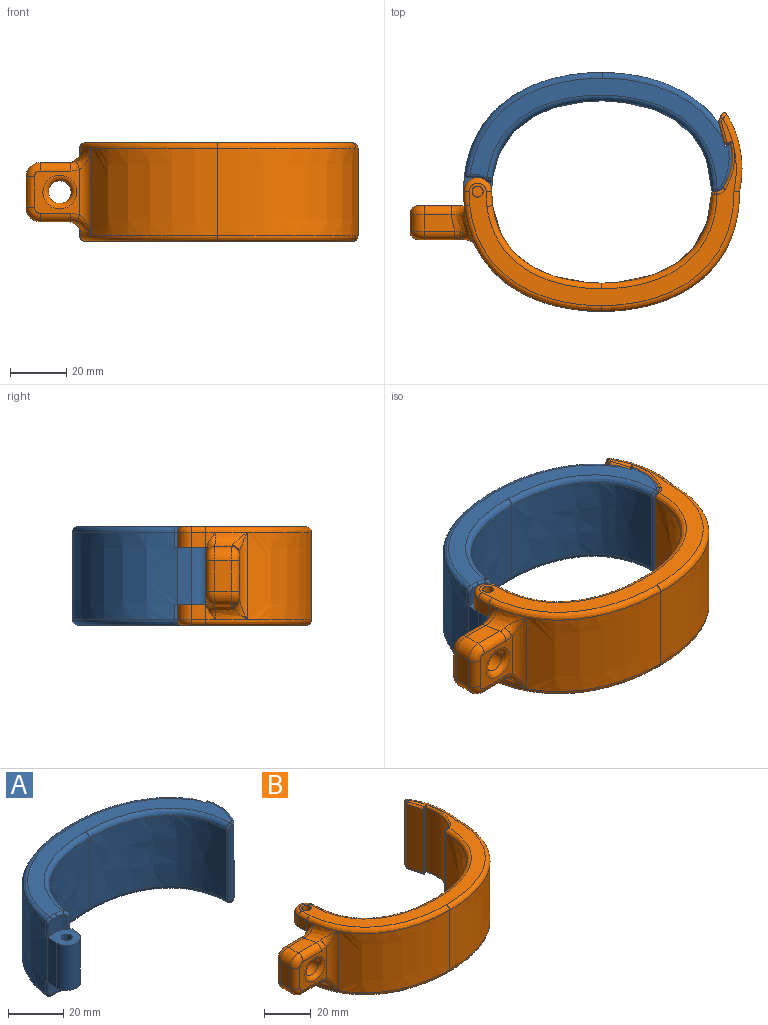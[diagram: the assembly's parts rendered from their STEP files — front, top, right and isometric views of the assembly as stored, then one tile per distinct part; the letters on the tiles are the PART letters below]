
ASSEMBLY  parts=2 mates=1
PART A: 57 faces, bbox 98.1x59.6x36.4 mm
  f0: extruded ~20x5mm, area 100.2mm2, adj f1,f12,f16,f19
  f1: cylinder r=5mm len=20mm, axis (0,0,-1), area 314.2mm2, adj f0,f3,f16,f19
  f2: cylinder r=1.95mm len=20mm, axis (0,0,-1), area 245mm2, adj f16,f19
  f3: extruded ~31x5mm, area 109.4mm2, adj f1,f4,f16,f19,f25,f30,f36,f42
  f4: extruded ~38.7x31mm, area 1624.9mm2, adj f3,f5,f24,f29
  f5: extruded ~38.98x31.03mm, area 1734.8mm2, adj f4,f23,f28,f47
  f6: plane 32.71x0.48mm, normal (0,-1,0), area 15.5mm2, adj f7,f46,f47,f49
  f7: cylinder r=3mm len=33mm, axis (0,0,-1), area 111.7mm2, adj f6,f8,f44,f45,f46,f49,f50,f51
  f8: cylinder r=20mm len=33mm, axis (0,0,-1), area 524.6mm2, adj f7,f43,f48,f54
  f9: plane 34.6x1.62mm, normal (-0.4,0.92,0), area 60.9mm2, adj f10,f52,f53,f54,f55,f56
  f10: plane 36.2x9.58mm, normal (0.96,0.27,0), area 292.8mm2, adj f9,f11,f13,f14,f22,f27,f52,f56
  f11: extruded ~41.39x31mm, area 1446.8mm2, adj f10,f12,f22,f27
  f12: extruded ~48.76x37.5mm, area 2099.6mm2, adj f0,f11,f16,f19,f21,f26,f31,f37
  f13: plane 91.85x39.01mm, normal (0,0,1), area 717.6mm2, adj f10,f26,f27,f28,f29,f30,f33,f34
  f14: plane 91.85x39.02mm, normal (0,0,-1), area 717.6mm2, adj f10,f21,f22,f23,f24,f25,f39,f40
  f15: plane 6.5x3.64mm, normal (0,-1,0), area 23.5mm2, adj f16,f17,f31,f32,f33
  f16: plane 11.2x10.29mm, normal (0,0,1), area 73.4mm2, adj f0,f1,f2,f3,f12,f15,f17,f31
  f17: cylinder r=5mm len=6.5mm, axis (0,0,-1), area 24.8mm2, adj f15,f16,f34,f35,f36
  f18: cylinder r=5mm len=6.5mm, axis (0,0,1), area 24.8mm2, adj f19,f20,f40,f41,f42
  f19: plane 11.2x10.29mm, normal (0,0,-1), area 73.4mm2, adj f0,f1,f2,f3,f12,f18,f20,f37
  f20: plane 6.5x3.64mm, normal (0,-1,0), area 23.5mm2, adj f18,f19,f37,f38,f39
  f21: bspline ~51.67x37.47mm, area 207mm2, adj f12,f14,f22,f38
  f22: bspline ~57.81x25.32mm, area 152.8mm2, adj f10,f11,f14,f21
  f23: bspline ~50.93x33.4mm, area 179.4mm2, adj f5,f14,f24,f49,f51
  f24: bspline ~50.38x45.92mm, area 168mm2, adj f4,f14,f23,f25
  f25: bspline ~2.68x2.27mm, area 1.9mm2, adj f3,f14,f24,f41
  f26: bspline ~51.67x37.47mm, area 207mm2, adj f12,f13,f27,f32
  f27: bspline ~57.81x25.32mm, area 152.8mm2, adj f10,f11,f13,f26
  f28: bspline ~50.93x33.4mm, area 179.4mm2, adj f5,f13,f29,f45,f46
  f29: bspline ~53.82x50.38mm, area 168mm2, adj f4,f13,f28,f30
  f30: bspline ~2.68x2.27mm, area 1.9mm2, adj f3,f13,f29,f35
  f31: cylinder r=1mm len=5.5mm, axis (0,0,-1), area 9.3mm2, adj f12,f15,f16,f32
  f32: bspline ~2.48x2.25mm, area 4.3mm2, adj f15,f26,f31,f33
  f33: cylinder r=1mm len=2.64mm, axis (-1,0,0), area 4.1mm2, adj f13,f15,f32,f34
  f34: torus R=6mm, axis (0,0,1), area 4.9mm2, adj f13,f17,f33,f35
  f35: bspline ~3.08x2.8mm, area 5.4mm2, adj f17,f30,f34,f36
  f36: cylinder r=1mm len=5.5mm, axis (0,0,-1), area 12.4mm2, adj f3,f16,f17,f35
  f37: cylinder r=1mm len=5.5mm, axis (0,0,-1), area 9.3mm2, adj f12,f19,f20,f38
  f38: bspline ~2.59x2.48mm, area 4.3mm2, adj f20,f21,f37,f39
  f39: cylinder r=1mm len=2.64mm, axis (1,0,0), area 4.1mm2, adj f14,f20,f38,f40
  f40: torus R=6mm, axis (0,0,1), area 4.9mm2, adj f14,f18,f39,f41
  f41: bspline ~3.08x2.8mm, area 5.4mm2, adj f18,f25,f40,f42
  f42: cylinder r=1mm len=5.5mm, axis (0,0,-1), area 12.4mm2, adj f3,f18,f19,f41
  f43: torus R=19mm, axis (0,0,1), area 24.4mm2, adj f8,f13,f44,f55
  f44: torus R=2mm, axis (0,0,1), area 3.8mm2, adj f7,f13,f43,f45
  f45: bspline ~1.62x1.19mm, area 1.4mm2, adj f7,f28,f44,f46
  f46: bspline ~1.96x1.67mm, area 2.7mm2, adj f6,f7,f28,f45,f47
  f47: cylinder r=1mm len=31mm, axis (0,0,-1), area 47.6mm2, adj f5,f6,f46,f49
  f48: torus R=19mm, axis (0,0,1), area 24.4mm2, adj f8,f14,f50,f53
  f49: bspline ~2.17x1.67mm, area 2.7mm2, adj f6,f7,f23,f47,f51
  f50: torus R=2mm, axis (0,0,1), area 3.8mm2, adj f7,f14,f48,f51
  f51: bspline ~1.62x1.19mm, area 1.4mm2, adj f7,f23,f49,f50
  f52: cylinder r=0.2mm len=0.98mm, axis (-0.92,-0.4,0), area 0.3mm2, adj f9,f10,f14,f53
  f53: bspline ~1.22x1.06mm, area 0.5mm2, adj f9,f48,f52,f54
  f54: cylinder r=0.2mm len=33mm, axis (0,0,-1), area 11.4mm2, adj f8,f9,f53,f55
  f55: bspline ~1.23x1.07mm, area 0.5mm2, adj f9,f43,f54,f56
  f56: cylinder r=0.2mm len=0.98mm, axis (0.92,0.4,0), area 0.3mm2, adj f9,f10,f13,f55
PART B: 97 faces, bbox 121.1x71.8x35.4 mm
  f0: cylinder r=1.95mm len=5.4mm, axis (0,0,-1), area 66.2mm2, adj f27,f91
  f1: plane 21x20.2mm, normal (0,1,0), area 229.3mm2, adj f5,f7,f26,f27,f28,f36,f37,f38
  f2: plane 16.17x15.98mm, normal (0,-1,0), area 125.9mm2, adj f34,f42,f43,f44,f45,f46,f71,f87
  f3: plane 8.62x3.93mm, normal (0,0,-1), area 13.3mm2, adj f56,f64,f65,f92
  f4: plane 8.62x3.93mm, normal (0,0,1), area 13.3mm2, adj f50,f68,f70,f96
  f5: extruded ~6.54x3.52mm, area 8.5mm2, adj f1,f9,f36,f60
  f6: extruded ~44.58x31mm, area 1634.5mm2, adj f13,f34,f54,f60
  f7: extruded ~6.54x3.52mm, area 8.5mm2, adj f1,f12,f40,f54
  f8: cylinder r=5mm len=10mm, axis (0,0,-1), area 84.8mm2, adj f9,f10,f27,f63
  f9: extruded ~5.4x5mm, area 27mm2, adj f5,f8,f27,f62
  f10: extruded ~31x5mm, area 117.1mm2, adj f8,f11,f22,f27,f28,f51,f61,f73
  f11: cylinder r=5mm len=10mm, axis (0,0,-1), area 84.8mm2, adj f10,f12,f28,f53
  f12: extruded ~5.4x5mm, area 27mm2, adj f7,f11,f28,f55
  f13: extruded ~49x42.5mm, area 2267.2mm2, adj f6,f14,f52,f58
  f14: cylinder r=38mm len=31mm, axis (0,0,-1), area 885.4mm2, adj f13,f50,f56,f67
  f15: extruded ~33x2.54mm, area 92.3mm2, adj f16,f65,f66,f67,f69,f70
  f16: plane 33x7.97mm, normal (-0.96,-0.27,0), area 273mm2, adj f15,f64,f68,f94
  f17: plane 34.94x2.69mm, normal (0.4,-0.92,0), area 61.2mm2, adj f18,f50,f74,f75,f83,f84,f92,f93
  f18: cylinder r=20mm len=33mm, axis (0,0,-1), area 554.5mm2, adj f17,f19,f75,f84
  f19: cylinder r=3mm len=33mm, axis (0,0,-1), area 98.3mm2, adj f18,f20,f76,f77,f81,f82
  f20: plane 32.69x0.47mm, normal (0,1,0), area 15.1mm2, adj f19,f78,f79,f80
  f21: extruded ~38.99x31.52mm, area 1750mm2, adj f22,f48,f57,f79
  f22: extruded ~38.7x31mm, area 1624.9mm2, adj f10,f21,f49,f59
  f23: cylinder r=1.95mm len=7.4mm, axis (0,0,-1), area 90.7mm2, adj f24,f28
  f24: plane 94.84x58.24mm, normal (0,0,1), area 805.7mm2, adj f23,f48,f49,f50,f51,f52,f53,f54
  f25: plane 94.84x58.24mm, normal (0,0,-1), area 817.6mm2, adj f56,f57,f58,f59,f60,f61,f62,f63
  f26: cylinder r=5mm len=20.2mm, axis (0,0,1), area 131.8mm2, adj f1,f27,f28,f73
  f27: plane 10.1x10.06mm, normal (0,0,1), area 71.7mm2, adj f0,f1,f8,f9,f10,f26,f73
  f28: plane 10.1x10.06mm, normal (0,0,-1), area 71.7mm2, adj f1,f10,f11,f12,f23,f26,f73
  f29: plane 10.85x6mm, normal (0,0,1), area 60.9mm2, adj f33,f39,f45,f86
  f30: plane 10.85x6mm, normal (0,0,-1), area 60.9mm2, adj f35,f37,f43,f89
  f31: plane 11x6mm, normal (-1,0,0), area 66mm2, adj f38,f44,f86,f89
  f32: cylinder r=4mm len=8mm, axis (0,1,0), area 201.1mm2, adj f71,f72
  f33: bspline ~18.34x10.21mm, area 65.8mm2, adj f29,f40,f46,f47,f54
  f34: cylinder r=5mm len=31mm, axis (0,0,-1), area 129.6mm2, adj f2,f6,f41,f47
  f35: bspline ~18.34x10.21mm, area 65.8mm2, adj f30,f36,f41,f42,f60
  f36: bspline ~9.93x9.45mm, area 31.9mm2, adj f1,f5,f35,f37
  f37: cylinder r=3mm len=9.57mm, axis (1,0,0), area 45.1mm2, adj f1,f30,f36,f88
  f38: cylinder r=3mm len=11mm, axis (0,0,-1), area 51.8mm2, adj f1,f31,f85,f88
  f39: cylinder r=3mm len=9.57mm, axis (-1,0,0), area 45.1mm2, adj f1,f29,f40,f85
  f40: bspline ~9.93x9.45mm, area 31.9mm2, adj f1,f7,f33,f39
  f41: bspline ~7.83x6.38mm, area 12.4mm2, adj f34,f35,f42
  f42: bspline ~6.7x3.9mm, area 11.4mm2, adj f2,f35,f41,f43
  f43: cylinder r=3mm len=10.85mm, axis (-1,0,0), area 51.1mm2, adj f2,f30,f42,f90
  f44: cylinder r=3mm len=11mm, axis (0,0,1), area 51.8mm2, adj f2,f31,f87,f90
  f45: cylinder r=3mm len=10.85mm, axis (1,0,0), area 51.1mm2, adj f2,f29,f46,f87
  f46: bspline ~6.7x3.9mm, area 11.4mm2, adj f2,f33,f45,f47
  f47: bspline ~7.83x6.38mm, area 12.4mm2, adj f33,f34,f46
  f48: bspline ~53.36x34.46mm, area 180.9mm2, adj f21,f24,f49,f80,f81
  f49: bspline ~50.38x45.92mm, area 168mm2, adj f22,f24,f48,f51
  f50: torus R=36mm, axis (0,0,1), area 87.5mm2, adj f4,f14,f17,f24,f52,f69,f83,f96
  f51: bspline ~6.4x2.33mm, area 16mm2, adj f10,f24,f49,f53
  f52: bspline ~63.46x43.9mm, area 226.5mm2, adj f13,f24,f50,f54
  f53: torus R=3mm, axis (0,0,1), area 42.2mm2, adj f11,f24,f51,f55
  f54: bspline ~62.59x60.72mm, area 210.7mm2, adj f6,f7,f24,f33,f52,f55
  f55: bspline ~6.11x2.25mm, area 15.5mm2, adj f12,f24,f53,f54
  f56: torus R=36mm, axis (0,0,1), area 87.5mm2, adj f3,f14,f25,f58,f66,f74
  f57: bspline ~53.36x34.46mm, area 180.9mm2, adj f21,f25,f59,f77,f78
  f58: bspline ~52.66x43.9mm, area 226.5mm2, adj f13,f25,f56,f60
  f59: bspline ~53.82x50.38mm, area 168mm2, adj f22,f25,f57,f61
  f60: bspline ~62.59x60.72mm, area 210.7mm2, adj f5,f6,f25,f35,f58,f62
  f61: bspline ~6.39x2.42mm, area 16mm2, adj f10,f25,f59,f63
  f62: bspline ~6.11x2.25mm, area 15.5mm2, adj f9,f25,f60,f63
  f63: torus R=3mm, axis (0,0,1), area 42.2mm2, adj f8,f25,f61,f62
  f64: cylinder r=1mm len=8.24mm, axis (0.27,-0.96,0), area 12.6mm2, adj f3,f16,f65,f93
  f65: bspline ~2.82x2.07mm, area 2.3mm2, adj f3,f15,f64,f66
  f66: bspline ~3.7x2.76mm, area 5.5mm2, adj f15,f56,f65,f67
  f67: cylinder r=1mm len=31mm, axis (0,0,-1), area 67.6mm2, adj f14,f15,f66,f69
  f68: cylinder r=1mm len=8.24mm, axis (-0.27,0.96,0), area 12.6mm2, adj f4,f16,f70,f95
  f69: bspline ~3.7x2.76mm, area 5.5mm2, adj f15,f50,f67,f70
  f70: bspline ~2.82x2.07mm, area 2.3mm2, adj f4,f15,f68,f69
  f71: torus R=6mm, axis (0,-1,0), area 93.3mm2, adj f2,f32
  f72: torus R=6mm, axis (0,-1,0), area 93.3mm2, adj f1,f32
  f73: cylinder r=1mm len=20.2mm, axis (0,0,-1), area 12.7mm2, adj f10,f26,f27,f28
  f74: bspline ~2.54x1.57mm, area 0.1mm2, adj f17,f56,f75,f92
  f75: torus R=21mm, axis (0,0,1), area 26.9mm2, adj f17,f18,f25,f74,f76
  f76: torus R=4mm, axis (0,0,1), area 4.5mm2, adj f19,f25,f75,f77
  f77: bspline ~1.87x1.3mm, area 1.3mm2, adj f19,f57,f76,f78
  f78: bspline ~2.34x1.67mm, area 2.6mm2, adj f20,f57,f77,f79
  f79: cylinder r=1mm len=31mm, axis (0,0,-1), area 48mm2, adj f20,f21,f78,f80
  f80: bspline ~2.2x1.52mm, area 2.6mm2, adj f20,f48,f79,f81
  f81: bspline ~1.53x1.3mm, area 1.3mm2, adj f19,f48,f80,f82
  f82: torus R=4mm, axis (0,0,1), area 4.5mm2, adj f19,f24,f81,f84
  f83: bspline ~2.54x1.57mm, area 0.1mm2, adj f17,f50,f84
  f84: torus R=21mm, axis (0,0,1), area 26.9mm2, adj f17,f18,f24,f82,f83
  f85: torus R=2mm, axis (0,-1,0), area 28.9mm2, adj f1,f38,f39,f86
  f86: cylinder r=5mm len=6mm, axis (0,1,0), area 47.1mm2, adj f29,f31,f85,f87
  f87: torus R=2mm, axis (0,-1,0), area 28.9mm2, adj f2,f44,f45,f86
  f88: torus R=2mm, axis (0,-1,0), area 28.9mm2, adj f1,f37,f38,f89
  f89: cylinder r=5mm len=6mm, axis (0,-1,0), area 47.1mm2, adj f30,f31,f88,f90
  f90: torus R=2mm, axis (0,-1,0), area 28.9mm2, adj f2,f43,f44,f89
  f91: plane 3.9x3.9mm, normal (0,0,1), area 11.9mm2, adj f0
  f92: cylinder r=0.2mm len=1.91mm, axis (0.92,0.4,0), area 0.5mm2, adj f3,f17,f74,f93
  f93: bspline ~1.17x1mm, area 0.5mm2, adj f17,f64,f92,f94
  f94: cylinder r=0.2mm len=33mm, axis (0,0,-1), area 11.2mm2, adj f16,f17,f93,f95
  f95: bspline ~1.17x1.05mm, area 0.5mm2, adj f17,f68,f94,f96
  f96: cylinder r=0.2mm len=1.91mm, axis (-0.92,-0.4,0), area 0.5mm2, adj f4,f17,f50,f95
PLACE A rot(axis=(0,0,-1),0.3deg) t=(0,-0.23,0.1)mm
PLACE B at identity fixed
MATE revolute B.f0 <-> A.f2  axis (0,0,-1) through (-44,0,10.1)mm
